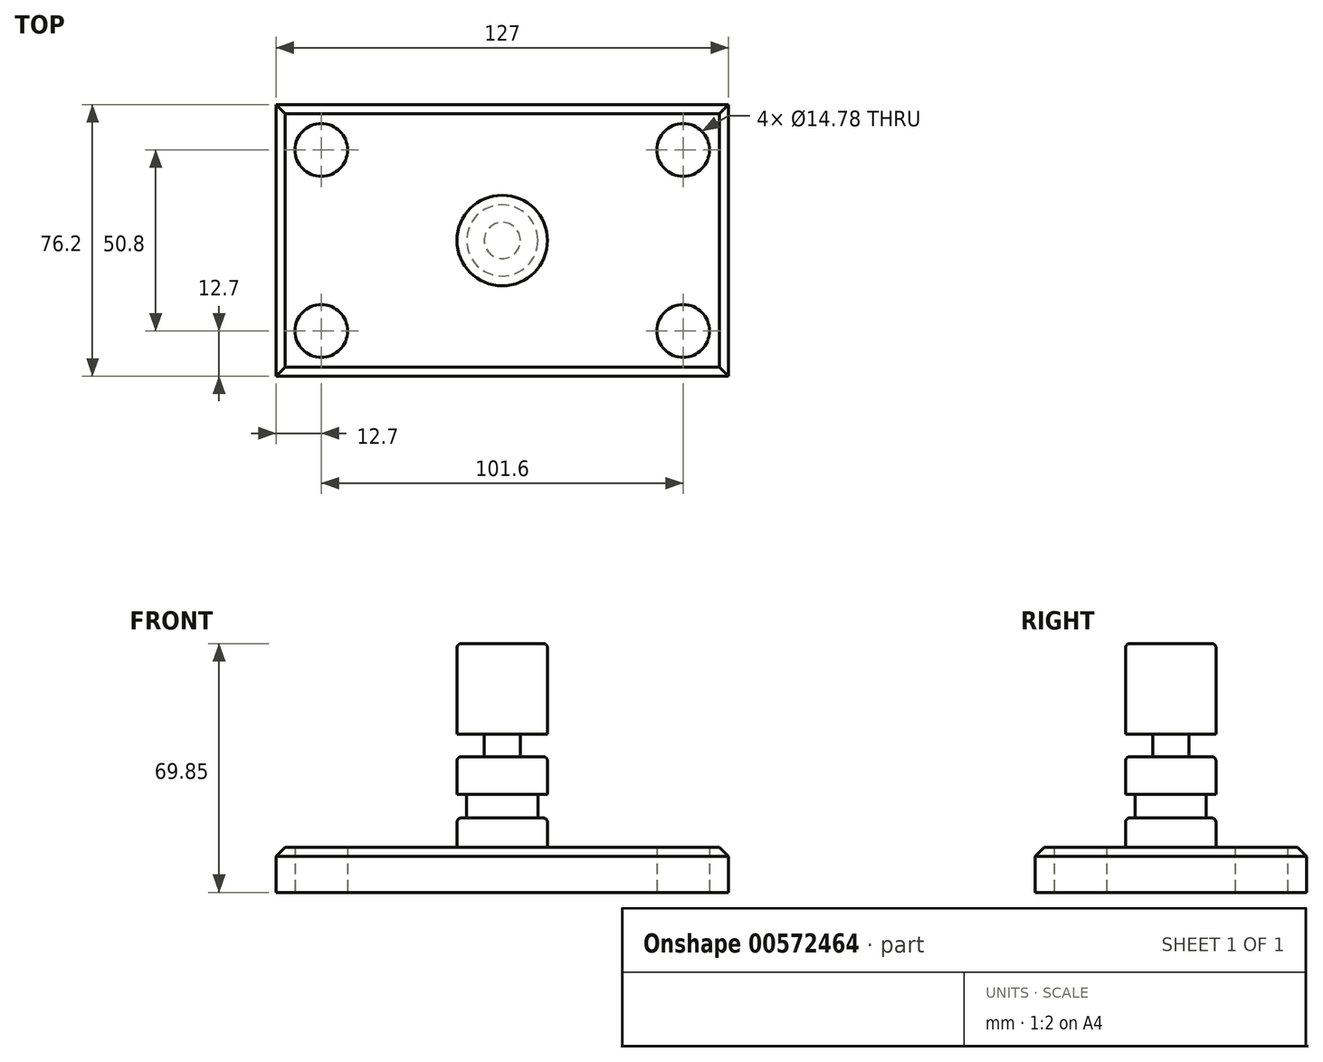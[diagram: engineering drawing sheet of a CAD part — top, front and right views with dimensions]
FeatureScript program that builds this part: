
annotation { "Feature Type Name" : "Feature", "Feature Type Description" : "" }
export const myFeature = defineFeature(function(context is Context, id is Id, definition is map)
    precondition{}
    {
        {
            var Q0;
            Q0=qCreatedBy(makeId("Top.planeOp"),FACE);
            var sketch = newSketch(context, id + "F0", { "sketchPlane" : qUnion([Q0])});
            skLineSegment(sketch, "E0.bottom", {"start": v(-63.5, 38.1) * mm, "end": v(63.5, 38.1) * mm});
            skLineSegment(sketch, "E0.top", {"start": v(-63.5, -38.1) * mm, "end": v(63.5, -38.1) * mm});
            skLineSegment(sketch, "E0.left", {"start": v(-63.5, 38.1) * mm, "end": v(-63.5, -38.1) * mm});
            skLineSegment(sketch, "E0.right", {"start": v(63.5, 38.1) * mm, "end": v(63.5, -38.1) * mm});
            skPoint(sketch, "E0.middle", {"position": v(0, 0) * mm});
            skCircle(sketch, "E1", {"center": v(-50.8, 25.4) * mm, "radius": 7.39 * mm});
            skCircle(sketch, "E2.MirrorC", {"center": v(50.8, 25.4) * mm, "radius": 7.39 * mm});
            skCircle(sketch, "E3.MirrorC", {"center": v(-50.8, -25.4) * mm, "radius": 7.39 * mm});
            skCircle(sketch, "E4.MirrorC", {"center": v(50.8, -25.4) * mm, "radius": 7.39 * mm});
            skSolve(sketch);
        }
        {
            var Q0;
            Q0=makeQuery(id+"F0.imprint","IMPRINT",FACE,{"disambiguationData":[TD([[makeQuery(id+"F0.imprint","IMPRINT",EDGE,{"derivedFrom":sQuery(id+"F0.wireOp",EDGE,"E0.bottom")}),-1.0]])]});
            extrude(context, id + "F1", {"entities" : qUnion([Q0]), "depth" : 12.7 * mm, "offsetDistance" : 25.4 * mm});
        }
        {
            var Q0;
            Q0=qCreatedBy(makeId("Front.planeOp"),FACE);
            var sketch = newSketch(context, id + "F2", { "sketchPlane" : qUnion([Q0])});
            skLineSegment(sketch, "E5.bottom", {"start": v(0, 38.1) * mm, "end": v(12.7, 38.1) * mm});
            skLineSegment(sketch, "E5.top", {"start": v(0, 12.7) * mm, "end": v(12.7, 12.7) * mm});
            skLineSegment(sketch, "E5.left", {"start": v(0, 38.1) * mm, "end": v(0, 12.7) * mm});
            skLineSegment(sketch, "E5.right", {"start": v(12.7, 38.1) * mm, "end": v(12.7, 12.7) * mm});
            skSolve(sketch);
        }
        {
            var Q0;
            Q0=makeQuery(id+"F2.imprint","IMPRINT",FACE,{"disambiguationData":[TD([[makeQuery(id+"F2.imprint","IMPRINT",EDGE,{"derivedFrom":sQuery(id+"F2.wireOp",EDGE,"E5.bottom")}),-1.0]])]});
            var Q1;
            Q1=sQuery(id+"F2.wireOp",EDGE,"E5.left");
            revolve(context, id + "F3", {"operationType" : NewBodyOperationType.ADD, "entities" : qUnion([Q0]), "axis" : qUnion([Q1]), "revolveType" : RevolveType.FULL});
        }
        {
            var Q0;
            Q0=qCreatedBy(makeId("Front.planeOp"),FACE);
            var sketch = newSketch(context, id + "F4", { "sketchPlane" : qUnion([Q0])});
            skLineSegment(sketch, "E6.bottom", {"start": v(0, 38.1) * mm, "end": v(5.08, 38.1) * mm});
            skLineSegment(sketch, "E6.top", {"start": v(0, 44.45) * mm, "end": v(5.08, 44.45) * mm});
            skLineSegment(sketch, "E6.left", {"start": v(0, 38.1) * mm, "end": v(0, 44.45) * mm});
            skLineSegment(sketch, "E6.right", {"start": v(5.08, 38.1) * mm, "end": v(5.08, 44.45) * mm});
            skSolve(sketch);
        }
        {
            var Q0;
            Q0 = qSketchRegion(id + "F4", true);
            var Q1;
            Q1=sQuery(id+"F4.wireOp",EDGE,"E6.left");
            revolve(context, id + "F5", {"operationType" : NewBodyOperationType.ADD, "entities" : qUnion([Q0]), "axis" : qUnion([Q1]), "revolveType" : RevolveType.FULL});
        }
        {
            var Q0;
            Q0=qCreatedBy(makeId("Front.planeOp"),FACE);
            var sketch = newSketch(context, id + "F6", { "sketchPlane" : qUnion([Q0])});
            skLineSegment(sketch, "E7.bottom", {"start": v(0, 69.85) * mm, "end": v(12.7, 69.85) * mm});
            skLineSegment(sketch, "E7.top", {"start": v(0, 44.45) * mm, "end": v(12.7, 44.45) * mm});
            skLineSegment(sketch, "E7.left", {"start": v(0, 69.85) * mm, "end": v(0, 44.45) * mm});
            skLineSegment(sketch, "E7.right", {"start": v(12.7, 69.85) * mm, "end": v(12.7, 44.45) * mm});
            skSolve(sketch);
        }
        {
            var Q0;
            Q0=makeQuery(id+"F6.imprint","IMPRINT",FACE,{"disambiguationData":[TD([[makeQuery(id+"F6.imprint","IMPRINT",EDGE,{"derivedFrom":sQuery(id+"F6.wireOp",EDGE,"E7.bottom")}),-1.0]])]});
            var Q1;
            Q1=sQuery(id+"F6.wireOp",EDGE,"E7.left");
            revolve(context, id + "F7", {"operationType" : NewBodyOperationType.ADD, "entities" : qUnion([Q0]), "axis" : qUnion([Q1]), "revolveType" : RevolveType.FULL});
        }
        {
            var Q0;
            Q0=qCreatedBy(makeId("Front.planeOp"),FACE);
            var sketch = newSketch(context, id + "F8", { "sketchPlane" : qUnion([Q0])});
            skLineSegment(sketch, "E8.bottom", {"start": v(9.98, 27.45) * mm, "end": v(18.58, 27.45) * mm});
            skLineSegment(sketch, "E8.top", {"start": v(9.98, 20.91) * mm, "end": v(18.58, 20.91) * mm});
            skLineSegment(sketch, "E8.left", {"start": v(9.98, 27.45) * mm, "end": v(9.98, 20.91) * mm});
            skLineSegment(sketch, "E8.right", {"start": v(18.58, 27.45) * mm, "end": v(18.58, 20.91) * mm});
            skSolve(sketch);
        }
        {
            var Q0;
            Q0=makeQuery(id+"F8.imprint","IMPRINT",FACE,{"disambiguationData":[TD([[makeQuery(id+"F8.imprint","IMPRINT",EDGE,{"derivedFrom":sQuery(id+"F8.wireOp",EDGE,"E8.bottom")}),-1.0]])]});
            var Q1;
            Q1=makeQuery(id+"F3.opRevolve","SWEPT_FACE",FACE,{"disambiguationData":[OSD([sQuery(id+"F2.wireOp",EDGE,"E5.right")])]});
            revolve(context, id + "F9", {"operationType" : NewBodyOperationType.REMOVE, "entities" : qUnion([Q0]), "axis" : qUnion([Q1]), "revolveType" : RevolveType.FULL, "oppositeDirection" : true});
        }
        {
            var Q0;
            Q0=makeQuery(id+"F7.opRevolve","SWEPT_EDGE",EDGE,{"disambiguationData":[OSD([sQuery(id+"F6.wireOp",EDGE,"E7.bottom"),sQuery(id+"F6.wireOp",EDGE,"E7.right")])]});
            fillet(context, id + "F10", {"entities" : qUnion([Q0]), "radius" : 1.27 * mm, "tangentPropagation" : true, "allowEdgeOverflow" : false});
        }
        {
            var Q0;
            Q0=makeQuery(id+"F1.opExtrude","CAP_EDGE",EDGE,{"disambiguationData":[OSD([sQuery(id+"F0.wireOp",EDGE,"E0.top")])],"isStart":false});
            var Q1;
            Q1=makeQuery(id+"F1.opExtrude","CAP_EDGE",EDGE,{"disambiguationData":[OSD([sQuery(id+"F0.wireOp",EDGE,"E0.left")])],"isStart":false});
            var Q2;
            Q2=makeQuery(id+"F1.opExtrude","CAP_EDGE",EDGE,{"disambiguationData":[OSD([sQuery(id+"F0.wireOp",EDGE,"E0.bottom")])],"isStart":false});
            var Q3;
            Q3=makeQuery(id+"F1.opExtrude","CAP_EDGE",EDGE,{"disambiguationData":[OSD([sQuery(id+"F0.wireOp",EDGE,"E0.right")])],"isStart":false});
            chamfer(context, id + "F11", {"entities" : qUnion([Q0, Q1, Q2, Q3]), "width" : 2.54 * mm, "tangentPropagation" : true});
        }
        {
            var Q0;
            Q0=makeQuery(id+"F3.opRevolve","SWEPT_EDGE",EDGE,{"disambiguationData":[OSD([sQuery(id+"F2.wireOp",EDGE,"E5.bottom"),sQuery(id+"F2.wireOp",EDGE,"E5.right")])]});
            var Q1;
            Q1=makeQuery(id+"F9.boolean.opBoolean","INTERSECT",EDGE,{"derivedFrom":[makeQuery(id+"F3.opRevolve","SWEPT_FACE",FACE,{"disambiguationData":[OSD([sQuery(id+"F2.wireOp",EDGE,"E5.right")])]}),makeQuery(id+"F9.opRevolve","SWEPT_FACE",FACE,{"disambiguationData":[OSD([sQuery(id+"F8.wireOp",EDGE,"E8.top")])]})]});
            fillet(context, id + "F12", {"entities" : qUnion([Q0, Q1]), "radius" : 1.27 * mm, "tangentPropagation" : true, "allowEdgeOverflow" : false});
        }
    });
